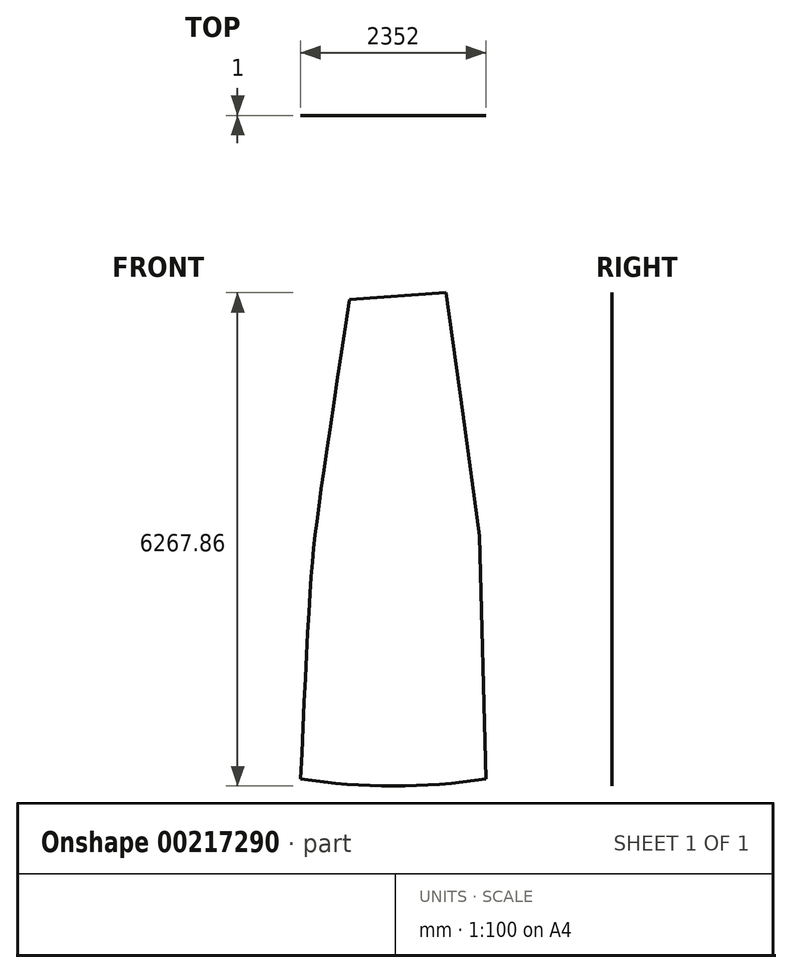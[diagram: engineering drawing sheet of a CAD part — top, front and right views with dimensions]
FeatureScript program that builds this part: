
annotation { "Feature Type Name" : "Feature", "Feature Type Description" : "" }
export const myFeature = defineFeature(function(context is Context, id is Id, definition is map)
    precondition{}
    {
        {
            var Q0;
            Q0=qCreatedBy(makeId("Front.planeOp"),FACE);
            var sketch = newSketch(context, id + "F0", { "sketchPlane" : qUnion([Q0])});
            skLineSegment(sketch, "E0", {"start": v(0, 0) * mm, "end": v(2352, 0) * mm});
            skLineSegment(sketch, "E1", {"start": v(0, 0) * mm, "end": v(620.2, 6088.5) * mm});
            skLineSegment(sketch, "E2", {"start": v(620.2, 6088.5) * mm, "end": v(2352, 0) * mm});
            skLineSegment(sketch, "E3", {"start": v(620.2, 6088.5) * mm, "end": v(1841.93, 6177.86) * mm});
            skLineSegment(sketch, "E4", {"start": v(1841.93, 6177.86) * mm, "end": v(2352, 0) * mm});
            skSolve(sketch);
        }
        {
            var Q0;
            Q0=makeQuery(id+"F0.imprint","IMPRINT",FACE,{"disambiguationData":[TD([[makeQuery(id+"F0.imprint","IMPRINT",EDGE,{"derivedFrom":sQuery(id+"F0.wireOp",EDGE,"E0")}),1.0]])]});
            var sketch = newSketch(context, id + "F1", { "sketchPlane" : qUnion([Q0])});
            skLineSegment(sketch, "E5", {"start": v(620.2, 6088.5) * mm, "end": v(1838.9, 5964.35) * mm});
            skLineSegment(sketch, "E6", {"start": v(1838.9, 5964.35) * mm, "end": v(2352, 0) * mm});
            skLineSegment(sketch, "E7", {"start": v(620.2, 6088.5) * mm, "end": v(2352, 0) * mm});
            skSolve(sketch);
        }
        {
            var Q0;
            Q0=makeQuery(id+"F0.imprint","IMPRINT",FACE,{"disambiguationData":[TD([[makeQuery(id+"F0.imprint","IMPRINT",EDGE,{"derivedFrom":sQuery(id+"F0.wireOp",EDGE,"E0")}),1.0]])]});
            var sketch = newSketch(context, id + "F2", { "sketchPlane" : qUnion([Q0])});
            skArc(sketch, "E8", {"start": v(0, 0) * mm, "mid": v(1176, -90) * mm, "end": v(2352, 0) * mm});
            skPoint(sketch, "E9", {"position": v(2096.97, 3088.93) * mm});
            skLineSegment(sketch, "E10", {"start": v(2096.97, 3088.93) * mm, "end": v(1841.93, 6177.86) * mm, "construction": true});
            skPoint(sketch, "E11", {"position": v(1969.45, 4633.4) * mm});
            skLineSegment(sketch, "E12", {"start": v(2268.6, 3088.93) * mm, "end": v(218.6, 3088.93) * mm, "construction": true});
            skLineSegment(sketch, "E13", {"start": v(2062.38, 4633.4) * mm, "end": v(452.38, 4633.4) * mm, "construction": true});
            skLineSegment(sketch, "E14", {"start": v(0, 0) * mm, "end": v(233.1, 3492.23) * mm, "construction": true});
            skLineSegment(sketch, "E15", {"start": v(1841.93, 6177.86) * mm, "end": v(2062.38, 4633.4) * mm});
            skLineSegment(sketch, "E16", {"start": v(2062.38, 4633.4) * mm, "end": v(2268.6, 3088.93) * mm});
            skLineSegment(sketch, "E17", {"start": v(2268.6, 3088.93) * mm, "end": v(2352, 0) * mm});
            skLineSegment(sketch, "E18", {"start": v(620.2, 6088.5) * mm, "end": v(1841.93, 6177.86) * mm});
            skFitSpline(sketch, "E19", {"points": [v(0, 0) * mm, v(127.67, 2496.74) * mm, v(233.1, 3492.23) * mm, v(620.2, 6088.5) * mm], "startDerivative": vector(340.46, 7570.42) * mm, "endDerivative": vector(1177.6, 7705.28) * mm});
            skSolve(sketch);
        }
        {
            var Q0;
            Q0 = qSketchRegion(id + "F2", true);
            extrude(context, id + "F3", {"entities" : qUnion([Q0]), "depth" : 1 * mm});
        }
    });
